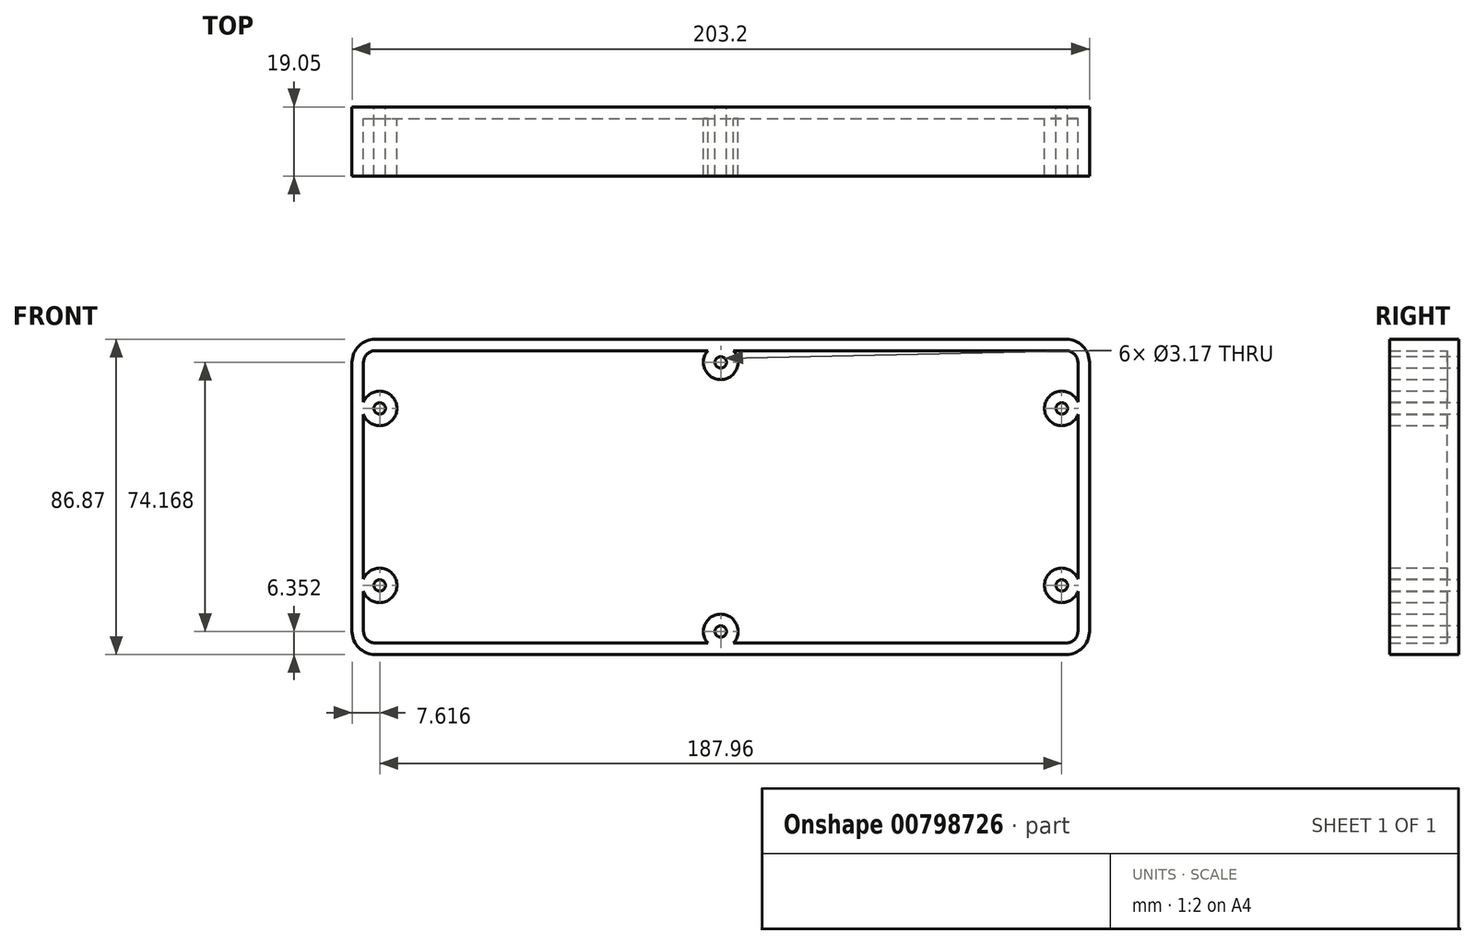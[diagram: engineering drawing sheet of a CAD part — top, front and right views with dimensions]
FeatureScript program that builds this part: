
annotation { "Feature Type Name" : "Feature", "Feature Type Description" : "" }
export const myFeature = defineFeature(function(context is Context, id is Id, definition is map)
    precondition{}
    {
        {
            var Q0;
            Q0=qCreatedBy(makeId("Front.planeOp"),FACE);
            var sketch = newSketch(context, id + "F0", { "sketchPlane" : qUnion([Q0])});
            skLineSegment(sketch, "E0", {"start": v(-120.15, 44.26) * mm, "end": v(70.35, 44.26) * mm});
            skLineSegment(sketch, "E1", {"start": v(-126.5, 37.91) * mm, "end": v(-126.5, -36.26) * mm});
            skLineSegment(sketch, "E2", {"start": v(-120.15, -42.6) * mm, "end": v(70.35, -42.6) * mm});
            skLineSegment(sketch, "E3", {"start": v(76.7, -36.26) * mm, "end": v(76.7, 37.91) * mm});
            skPoint(sketch, "E4.center", {"position": v(20.3, 0.43) * mm});
            skCircle(sketch, "E5", {"center": v(-118.88, 25.21) * mm, "radius": 1.59 * mm});
            skCircle(sketch, "E6", {"center": v(-118.88, -23.56) * mm, "radius": 1.59 * mm});
            skCircle(sketch, "E7", {"center": v(-24.9, 37.91) * mm, "radius": 1.59 * mm});
            skCircle(sketch, "E8", {"center": v(-24.9, -36.26) * mm, "radius": 1.59 * mm});
            skCircle(sketch, "E9", {"center": v(69.08, 25.21) * mm, "radius": 1.59 * mm});
            skCircle(sketch, "E10", {"center": v(69.08, -23.56) * mm, "radius": 1.59 * mm});
            skPoint(sketch, "E11.visualSharp", {"position": v(-126.5, 44.26) * mm});
            skArc(sketch, "E11.filletArc", {"start": v(-120.15, 44.26) * mm, "mid": v(-124.64, 42.4) * mm, "end": v(-126.5, 37.91) * mm});
            skPoint(sketch, "E12.visualSharp", {"position": v(-126.5, -42.6) * mm});
            skArc(sketch, "E12.filletArc", {"start": v(-126.5, -36.26) * mm, "mid": v(-124.64, -40.75) * mm, "end": v(-120.15, -42.6) * mm});
            skPoint(sketch, "E13.visualSharp", {"position": v(76.7, -42.6) * mm});
            skArc(sketch, "E13.filletArc", {"start": v(70.35, -42.6) * mm, "mid": v(74.84, -40.75) * mm, "end": v(76.7, -36.26) * mm});
            skPoint(sketch, "E14.visualSharp", {"position": v(76.7, 44.26) * mm});
            skArc(sketch, "E14.filletArc", {"start": v(76.7, 37.91) * mm, "mid": v(74.84, 42.4) * mm, "end": v(70.35, 44.26) * mm});
            skSolve(sketch);
        }
        {
            var Q0;
            Q0 = qSketchRegion(id + "F0", true);
            extrude(context, id + "F1", {"entities" : qUnion([Q0]), "depth" : 19.05 * mm, "offsetDistance" : 25.4 * mm});
        }
        {
            var Q0;
            Q0=makeQuery(id+"F1.opExtrude","CAP_FACE",FACE,{"disambiguationData":[OSD([sQuery(id+"F0.wireOp",EDGE,"E0"),sQuery(id+"F0.wireOp",EDGE,"E1"),sQuery(id+"F0.wireOp",EDGE,"E2"),sQuery(id+"F0.wireOp",EDGE,"E3"),sQuery(id+"F0.wireOp",EDGE,"E5"),sQuery(id+"F0.wireOp",EDGE,"E6"),sQuery(id+"F0.wireOp",EDGE,"E7"),sQuery(id+"F0.wireOp",EDGE,"E8"),sQuery(id+"F0.wireOp",EDGE,"E9"),sQuery(id+"F0.wireOp",EDGE,"E10"),sQuery(id+"F0.wireOp",EDGE,"E11.filletArc"),sQuery(id+"F0.wireOp",EDGE,"E12.filletArc"),sQuery(id+"F0.wireOp",EDGE,"E13.filletArc"),sQuery(id+"F0.wireOp",EDGE,"E14.filletArc")])],"isStart":false});
            var Q1;
            Q1=makeQuery(id+"F1.opExtrude","SWEPT_BODY",BODY,{"disambiguationData":[OSD([sQuery(id+"F0.wireOp",EDGE,"E0"),sQuery(id+"F0.wireOp",EDGE,"E1"),sQuery(id+"F0.wireOp",EDGE,"E2"),sQuery(id+"F0.wireOp",EDGE,"E3"),sQuery(id+"F0.wireOp",EDGE,"E5"),sQuery(id+"F0.wireOp",EDGE,"E6"),sQuery(id+"F0.wireOp",EDGE,"E7"),sQuery(id+"F0.wireOp",EDGE,"E8"),sQuery(id+"F0.wireOp",EDGE,"E9"),sQuery(id+"F0.wireOp",EDGE,"E10"),sQuery(id+"F0.wireOp",EDGE,"E11.filletArc"),sQuery(id+"F0.wireOp",EDGE,"E12.filletArc"),sQuery(id+"F0.wireOp",EDGE,"E13.filletArc"),sQuery(id+"F0.wireOp",EDGE,"E14.filletArc")])]});
            shell(context, id + "F2", {"entities" : qUnion([Q0]), "parts" : qUnion([Q1]), "thickness" : 3.17 * mm});
        }
    });
